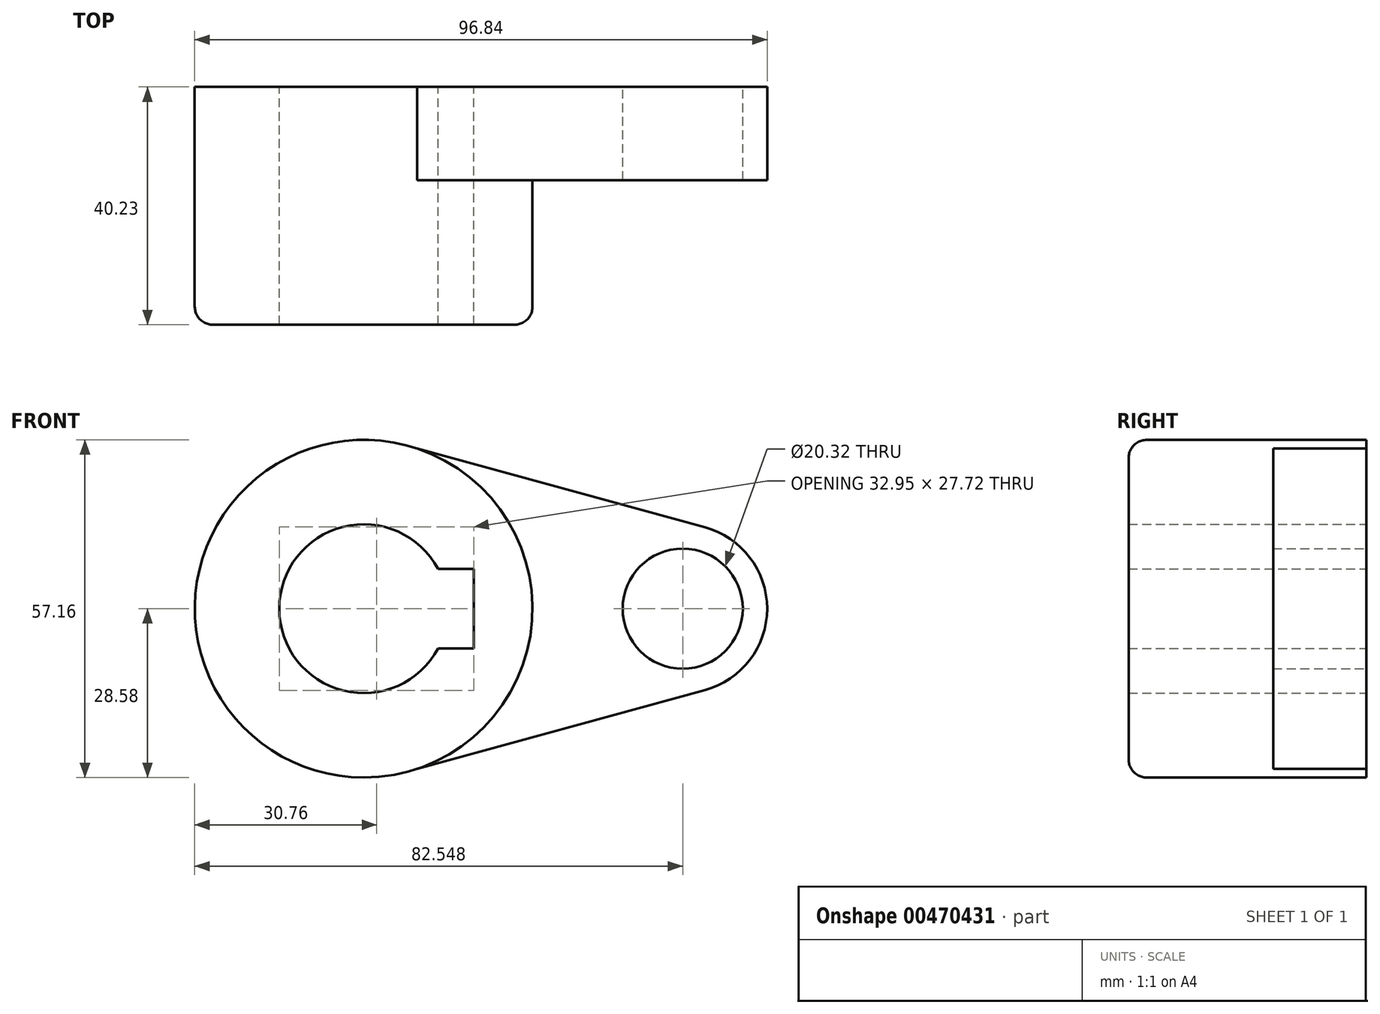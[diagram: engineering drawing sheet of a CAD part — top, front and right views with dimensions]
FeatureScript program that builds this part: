
annotation { "Feature Type Name" : "Feature", "Feature Type Description" : "" }
export const myFeature = defineFeature(function(context is Context, id is Id, definition is map)
    precondition{}
    {
        {
            var Q0;
            Q0=qCreatedBy(makeId("Front.planeOp"),FACE);
            var sketch = newSketch(context, id + "F0", { "sketchPlane" : qUnion([Q0])});
            skArc(sketch, "E0", {"start": v(-0.72, 9.92) * mm, "mid": v(-56.08, -0.88) * mm, "end": v(-0.16, -8.25) * mm});
            skArc(sketch, "E1", {"start": v(-14.9, 6.72) * mm, "mid": v(-41.8, 0) * mm, "end": v(-14.9, -6.72) * mm});
            skCircle(sketch, "E2", {"center": v(26.46, 0) * mm, "radius": 10.16 * mm});
            skArc(sketch, "E3", {"start": v(30.23, -13.78) * mm, "mid": v(40.75, 0) * mm, "end": v(30.23, 13.78) * mm});
            skLineSegment(sketch, "E4", {"start": v(-18.49, -27.11) * mm, "end": v(30.23, -13.78) * mm});
            skLineSegment(sketch, "E5", {"start": v(-18.49, 27.11) * mm, "end": v(30.23, 13.78) * mm});
            skArc(sketch, "E6", {"start": v(-0.16, -8.25) * mm, "mid": v(1.04, 0.88) * mm, "end": v(-0.72, 9.92) * mm});
            skLineSegment(sketch, "E7.bottom", {"start": v(-8.86, -6.72) * mm, "end": v(-14.9, -6.72) * mm});
            skLineSegment(sketch, "E7.top", {"start": v(-8.86, 6.72) * mm, "end": v(-14.9, 6.72) * mm});
            skLineSegment(sketch, "E7.left", {"start": v(-8.86, -6.72) * mm, "end": v(-8.86, 6.72) * mm});
            skPoint(sketch, "E7.right.end.orphan", {"position": v(-46.18, 6.72) * mm});
            skPoint(sketch, "E8.orphan", {"position": v(-46.18, -6.72) * mm});
            skSolve(sketch);
        }
        {
            var Q0;
            Q0=makeQuery(id+"F0.imprint","IMPRINT",FACE,{"disambiguationData":[TD([[makeQuery(id+"F0.imprint","IMPRINT",EDGE,{"derivedFrom":sQuery(id+"F0.wireOp",EDGE,"E2")}),-1.0]])]});
            extrude(context, id + "F1", {"entities" : qUnion([Q0]), "depth" : 15.77 * mm});
        }
        {
            var Q0;
            Q0=makeQuery(id+"F0.imprint","IMPRINT",FACE,{"disambiguationData":[TD([[makeQuery(id+"F0.imprint","IMPRINT",EDGE,{"derivedFrom":sQuery(id+"F0.wireOp",EDGE,"E1")}),-1.0]])]});
            extrude(context, id + "F2", {"entities" : qUnion([Q0]), "operationType" : NewBodyOperationType.ADD, "depth" : 40.23 * mm});
        }
        {
            var Q0;
            Q0=makeQuery(id+"F2.opExtrude","CAP_EDGE",EDGE,{"disambiguationData":[OSD([sQuery(id+"F0.wireOp",EDGE,"E0"),sQuery(id+"F0.wireOp",EDGE,"E6")])],"isStart":false});
            fillet(context, id + "F3", {"entities" : qUnion([Q0]), "radius" : 3.07 * mm, "tangentPropagation" : true, "allowEdgeOverflow" : false});
        }
    });
